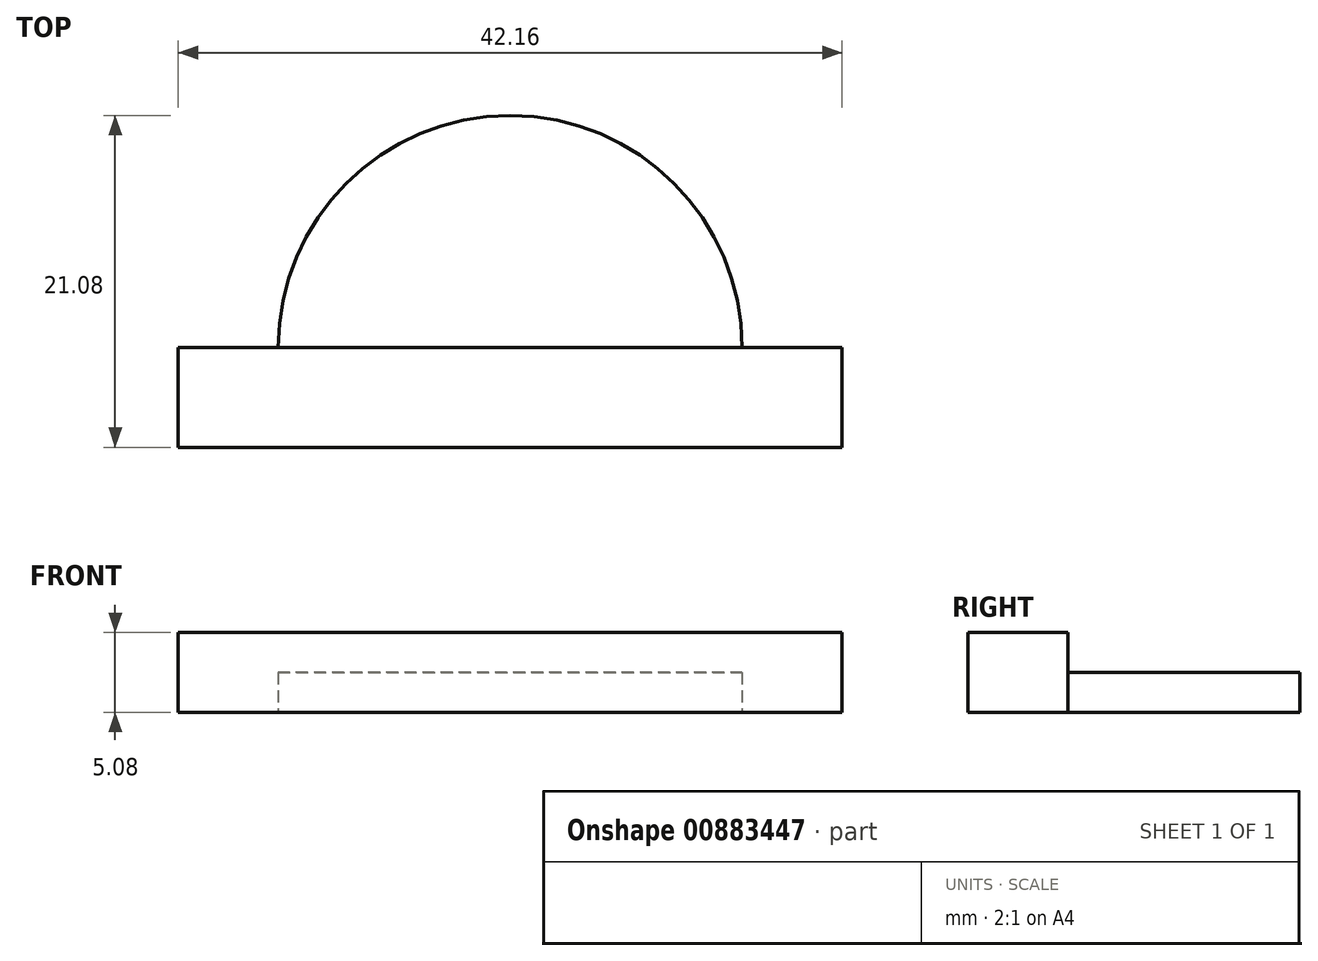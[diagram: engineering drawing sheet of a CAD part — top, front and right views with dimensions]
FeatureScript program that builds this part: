
annotation { "Feature Type Name" : "Feature", "Feature Type Description" : "" }
export const myFeature = defineFeature(function(context is Context, id is Id, definition is map)
    precondition{}
    {
        {
            var Q0;
            Q0=qCreatedBy(makeId("Top.planeOp"),FACE);
            var sketch = newSketch(context, id + "F0", { "sketchPlane" : qUnion([Q0])});
            skArc(sketch, "E0", {"start": v(14.73, 0) * mm, "mid": v(0, 14.73) * mm, "end": v(-14.73, 0) * mm});
            skLineSegment(sketch, "E1", {"start": v(-14.73, 0) * mm, "end": v(14.73, 0) * mm});
            skPoint(sketch, "E2.orphan", {"position": v(-30.36, 0) * mm});
            skSolve(sketch);
        }
        {
            var Q0;
            Q0=makeQuery(id+"F0.imprint","IMPRINT",FACE,{"disambiguationData":[TD([[makeQuery(id+"F0.imprint","IMPRINT",EDGE,{"derivedFrom":sQuery(id+"F0.wireOp",EDGE,"E0")}),1.0]])]});
            extrude(context, id + "F1", {"entities" : qUnion([Q0]), "depth" : 2.54 * mm, "offsetDistance" : 25.4 * mm});
        }
        {
            var Q0;
            Q0=qCreatedBy(makeId("Top.planeOp"),FACE);
            var sketch = newSketch(context, id + "F2", { "sketchPlane" : qUnion([Q0])});
            skLineSegment(sketch, "E3.bottom", {"start": v(-21.08, 0) * mm, "end": v(21.08, 0) * mm});
            skLineSegment(sketch, "E3.top", {"start": v(-21.08, -6.35) * mm, "end": v(21.08, -6.35) * mm});
            skLineSegment(sketch, "E3.left", {"start": v(-21.08, 0) * mm, "end": v(-21.08, -6.35) * mm});
            skLineSegment(sketch, "E3.right", {"start": v(21.08, 0) * mm, "end": v(21.08, -6.35) * mm});
            skSolve(sketch);
        }
        {
            var Q0;
            Q0=makeQuery(id+"F2.imprint","IMPRINT",FACE,{"disambiguationData":[TD([[makeQuery(id+"F2.imprint","IMPRINT",EDGE,{"derivedFrom":sQuery(id+"F2.wireOp",EDGE,"E3.bottom")}),-1.0]])]});
            extrude(context, id + "F3", {"entities" : qUnion([Q0]), "operationType" : NewBodyOperationType.ADD, "depth" : 5.08 * mm, "offsetDistance" : 25.4 * mm});
        }
    });
